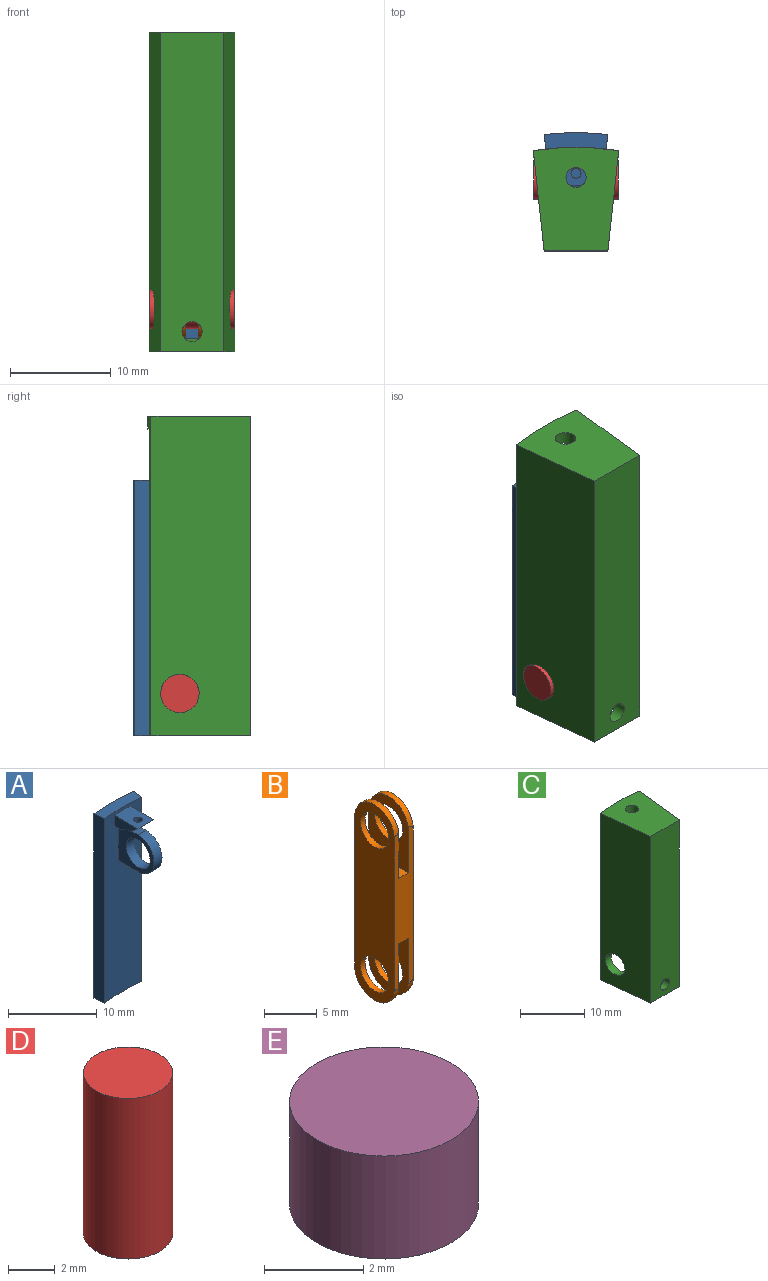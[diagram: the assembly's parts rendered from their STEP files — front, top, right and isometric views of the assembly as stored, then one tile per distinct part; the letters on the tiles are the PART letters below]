
ASSEMBLY  parts=5 mates=4
PART A: 20 faces, bbox 6.3x7.2x25.4 mm
  f0: plane 2.54x1.17mm, normal (0,-0.64,-0.77), area 3.5mm2, adj f3,f16,f17,f18,f19
  f1: plane 1.03x0.64mm, normal (0,0,-1), area 0.6mm2, adj f4,f14,f17,f18
  f2: plane 1.03x0.64mm, normal (0,0,-1), area 0.6mm2, adj f3,f4,f15,f18
  f3: plane 3.76x1.47mm, normal (-1,0,0), area 3.8mm2, adj f0,f2,f4,f16,f18
  f4: cylinder r=27.5mm len=25.4mm, axis (0,0,-1), area 142.2mm2, adj f1,f2,f3,f6,f7,f9,f10,f12
  f5: plane 2.14x1.27mm, normal (0,0,1), area 2.7mm2, adj f11,f14,f15,f18
  f6: plane 25.4x1.49mm, normal (-0.99,-0.11,0), area 38.1mm2, adj f4,f8,f9,f10
  f7: plane 25.4x1.49mm, normal (0.99,-0.12,0), area 38.1mm2, adj f4,f8,f9,f10
  f8: cylinder r=29mm len=25.4mm, axis (0,0,-1), area 161.1mm2, adj f6,f7,f9,f10
  f9: plane 6.33x1.66mm, normal (0,0,1), area 9.3mm2, adj f4,f6,f7,f8
  f10: plane 6.33x1.66mm, normal (0,0,-1), area 9.3mm2, adj f4,f6,f7,f8
  f11: cylinder r=2.54mm len=5.08mm, axis (-1,0,0), area 10.1mm2, adj f5,f12,f14,f15
  f12: plane 3.19x1.28mm, normal (0,0,-1), area 4mm2, adj f4,f11,f14,f15
  f13: cylinder r=1.91mm len=3.81mm, axis (-1,0,0), area 15.2mm2, adj f14,f15
  f14: plane 5.73x5.09mm, normal (1,0,0), area 14.9mm2, adj f1,f4,f5,f11,f12,f13
  f15: plane 5.73x5.09mm, normal (-1,0,0), area 14.9mm2, adj f2,f4,f5,f11,f12,f13
  f16: plane 3.79x2.54mm, normal (0,0,1), area 8.8mm2, adj f0,f3,f4,f17,f19
  f17: plane 3.76x1.47mm, normal (1,0,0), area 3.8mm2, adj f0,f1,f4,f16,f18
  f18: cylinder r=2.55mm len=2.54mm, axis (1,0,0), area 3.8mm2, adj f0,f1,f2,f3,f5,f17,f19
  f19: cylinder r=0.5mm len=1.03mm, axis (0,0,1), area 2.8mm2, adj f0,f16,f18
PART B: 18 faces, bbox 2.5x5.3x22.8 mm
  f0: cylinder r=22.2mm len=18.24mm, axis (0,0,-1), area 32.5mm2, adj f1,f3,f4,f5,f6,f7,f8,f11
  f1: plane 22.81x5.31mm, normal (1,0,0), area 92.2mm2, adj f0,f2,f7,f10,f15,f17
  f2: cylinder r=27.5mm len=18.16mm, axis (0,0,-1), area 32.4mm2, adj f1,f3,f4,f5,f6,f7,f8,f11
  f3: plane 22.81x5.31mm, normal (-1,0,0), area 92.2mm2, adj f0,f2,f8,f9,f14,f16
  f4: plane 7.59x5.3mm, normal (-1,0,0), area 25.9mm2, adj f0,f2,f6,f7,f10
  f5: plane 7.59x5.3mm, normal (1,0,0), area 25.9mm2, adj f0,f2,f6,f8,f9
  f6: plane 5.31x1.27mm, normal (0,0,-1), area 6.7mm2, adj f0,f2,f4,f5
  f7: cylinder r=2.66mm len=5.33mm, axis (1,0,0), area 5mm2, adj f0,f1,f2,f4
  f8: cylinder r=2.66mm len=5.33mm, axis (1,0,0), area 5mm2, adj f0,f2,f3,f5
  f9: cylinder r=1.91mm len=3.81mm, axis (1,0,0), area 7.6mm2, adj f3,f5
  f10: cylinder r=1.91mm len=3.81mm, axis (1,0,0), area 7.6mm2, adj f1,f4
  f11: plane 7.59x5.3mm, normal (-1,0,0), area 25.9mm2, adj f0,f2,f13,f15,f17
  f12: plane 7.59x5.3mm, normal (1,0,0), area 25.9mm2, adj f0,f2,f13,f14,f16
  f13: plane 5.31x1.27mm, normal (0,0,1), area 6.7mm2, adj f0,f2,f11,f12
  f14: cylinder r=2.66mm len=5.33mm, axis (1,0,0), area 5mm2, adj f0,f2,f3,f12
  f15: cylinder r=2.66mm len=5.33mm, axis (1,0,0), area 5mm2, adj f0,f1,f2,f11
  f16: cylinder r=1.91mm len=3.81mm, axis (1,0,0), area 7.6mm2, adj f3,f12
  f17: cylinder r=1.91mm len=3.81mm, axis (1,0,0), area 7.6mm2, adj f1,f11
PART C: 16 faces, bbox 8.5x10.3x31.8 mm
  f0: plane 30.48x8.84mm, normal (0.99,0.11,0), area 258.5mm2, adj f4,f6,f7,f9,f11,f14,f15
  f1: plane 31.75x9.94mm, normal (-0.99,-0.11,0), area 306mm2, adj f2,f4,f7,f8,f11
  f2: plane 31.75x6.33mm, normal (0,-1,0), area 197.8mm2, adj f1,f3,f7,f8,f12
  f3: plane 31.75x9.94mm, normal (0.99,-0.11,0), area 306mm2, adj f2,f4,f7,f8,f10
  f4: cylinder r=27.5mm len=31.75mm, axis (0,0,-1), area 88.3mm2, adj f0,f1,f3,f5,f7,f8,f9
  f5: plane 30.48x8.84mm, normal (-0.99,0.11,0), area 258.5mm2, adj f4,f6,f7,f9,f10,f14,f15
  f6: plane 30.48x4.05mm, normal (0,1,0), area 120.3mm2, adj f0,f5,f7,f9,f12
  f7: plane 10.11x8.5mm, normal (0,0,-1), area 38.7mm2, adj f0,f1,f2,f3,f4,f5,f6,f14
  f8: plane 10.27x8.5mm, normal (0,0,1), area 72.4mm2, adj f1,f2,f3,f4,f13
  f9: plane 9x5.99mm, normal (0,0,-1), area 41.9mm2, adj f0,f4,f5,f6,f13
  f10: cylinder r=1.91mm len=3.81mm, axis (-1,0,0), area 15.3mm2, adj f3,f5
  f11: cylinder r=1.91mm len=3.81mm, axis (-1,0,0), area 15.3mm2, adj f0,f1
  f12: cylinder r=1mm len=2mm, axis (0,1,0), area 8mm2, adj f2,f6
  f13: cylinder r=1mm len=2mm, axis (0,0,-1), area 8mm2, adj f8,f9
  f14: plane 5.49x1.52mm, normal (0,0.64,0.77), area 10.6mm2, adj f0,f5,f7,f15
  f15: plane 5.16x1.28mm, normal (0,-1,0), area 6.6mm2, adj f0,f5,f7,f14
PART D: 3 faces, bbox 3.8x3.8x8.4 mm
  f0: cylinder r=1.91mm len=8.38mm, axis (0,0,-1), area 100.3mm2, adj f1,f2
  f1: plane 3.81x3.81mm, normal (0,0,1), area 11.4mm2, adj f0
  f2: plane 3.81x3.81mm, normal (0,0,-1), area 11.4mm2, adj f0
PART E: 3 faces, bbox 3.8x3.8x2.5 mm
  f0: cylinder r=1.91mm len=3.81mm, axis (0,0,-1), area 30.4mm2, adj f1,f2
  f1: plane 3.81x3.81mm, normal (0,0,1), area 11.4mm2, adj f0
  f2: plane 3.81x3.81mm, normal (0,0,-1), area 11.4mm2, adj f0
PLACE A t=(-13.96,-1.03,-3.59)mm
PLACE B t=(-13.96,-24.66,-2.45)mm
PLACE C t=(-13.95,-0.99,-3.59)mm fixed
PLACE D rot(axis=(0,-1,0),90deg) t=(-9.76,0.16,0.6)mm fixed
PLACE E rot(axis=(0,-1,0),90deg) t=(-12.68,0.16,17.36)mm
MATE revolute D.f0 <-> B.f9  axis (1,0,0) through (-13.96,0.16,0.6)mm
MATE revolute A.f11 <-> B.f16  axis (-1,0,0) through (-14.59,0.16,17.36)mm
MATE parallel C.f7 <-> A.f10  axis (0,0,-1) through (-13.95,-2.01,-3.59)mm
MATE fastened E.f0 <-> B.f16  axis (-1,0,0) through (-15.22,0.16,17.36)mm
